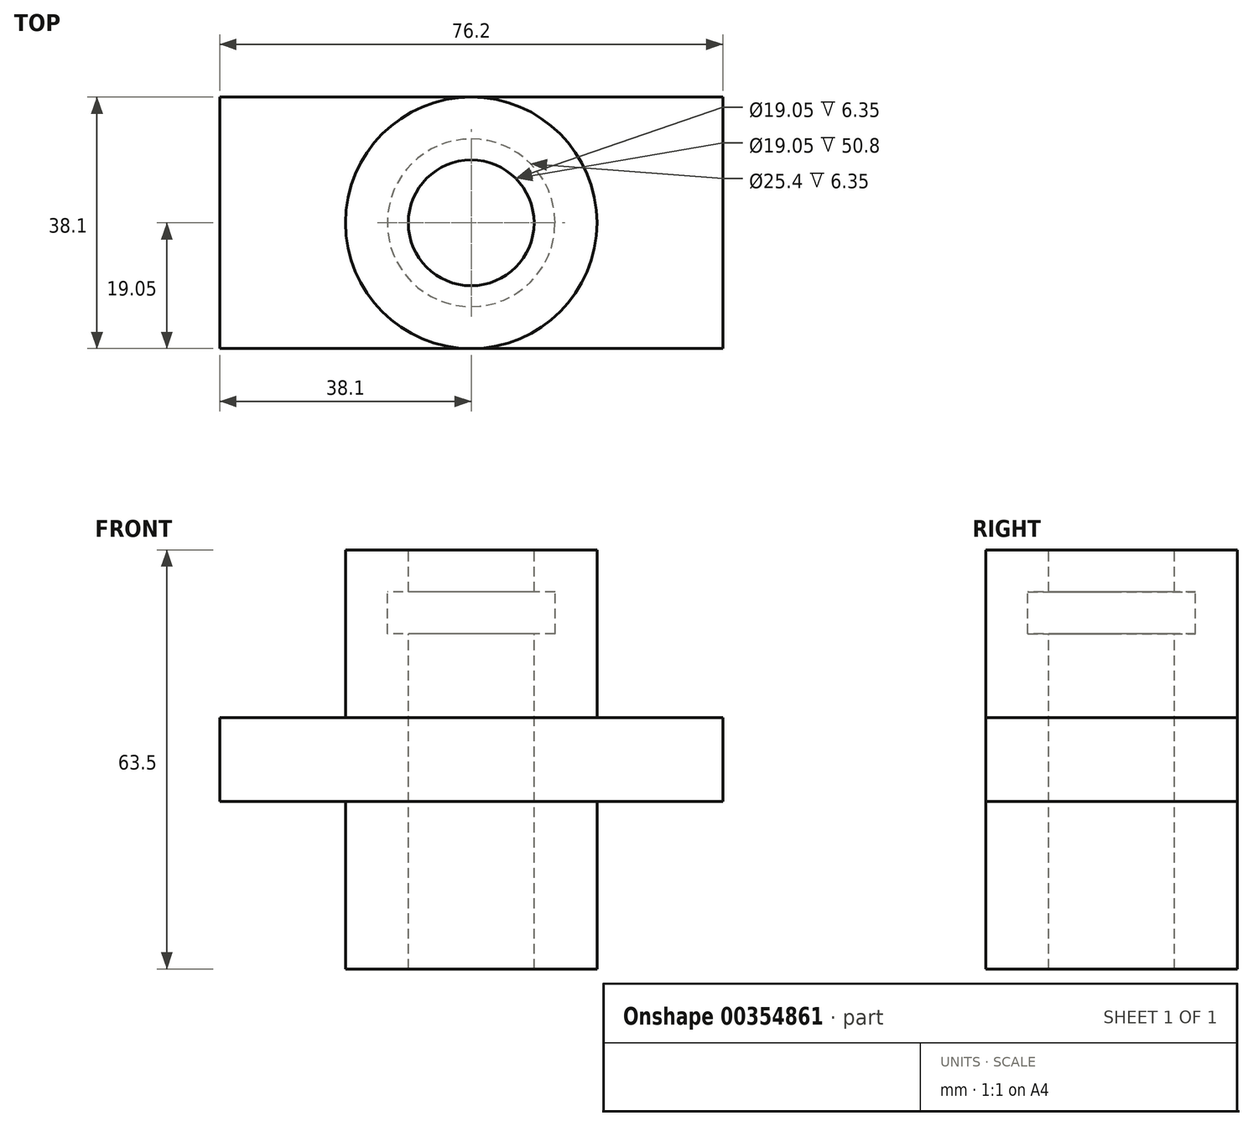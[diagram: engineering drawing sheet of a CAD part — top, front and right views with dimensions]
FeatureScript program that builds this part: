
annotation { "Feature Type Name" : "Feature", "Feature Type Description" : "" }
export const myFeature = defineFeature(function(context is Context, id is Id, definition is map)
    precondition{}
    {
        {
            var Q0;
            Q0=qCreatedBy(makeId("Front.planeOp"),FACE);
            var sketch = newSketch(context, id + "F0", { "sketchPlane" : qUnion([Q0])});
            skLineSegment(sketch, "E0", {"start": v(-9.53, 31.75) * mm, "end": v(-9.52, 25.4) * mm});
            skLineSegment(sketch, "E1", {"start": v(-9.53, 25.4) * mm, "end": v(-12.7, 25.4) * mm});
            skLineSegment(sketch, "E2", {"start": v(-12.7, 25.4) * mm, "end": v(-12.7, 19.05) * mm});
            skLineSegment(sketch, "E3", {"start": v(-12.7, 19.05) * mm, "end": v(-9.53, 19.05) * mm});
            skLineSegment(sketch, "E4", {"start": v(-9.53, 19.05) * mm, "end": v(-9.53, -31.75) * mm});
            skLineSegment(sketch, "E5", {"start": v(-9.53, -31.75) * mm, "end": v(-19.05, -31.75) * mm});
            skLineSegment(sketch, "E6", {"start": v(-19.05, -31.75) * mm, "end": v(-19.05, 31.75) * mm});
            skLineSegment(sketch, "E7", {"start": v(-19.05, 31.75) * mm, "end": v(-9.53, 31.75) * mm});
            skLineSegment(sketch, "E8", {"start": v(0, 58.37) * mm, "end": v(0, -55.1) * mm, "construction": true});
            skSolve(sketch);
        }
        {
            var Q0;
            Q0=makeQuery(id+"F0.imprint","IMPRINT",FACE,{"disambiguationData":[TD([[makeQuery(id+"F0.imprint","IMPRINT",EDGE,{"derivedFrom":sQuery(id+"F0.wireOp",EDGE,"E0")}),-1.0]])]});
            var Q1;
            Q1=sQuery(id+"F0.wireOp",EDGE,"E8");
            revolve(context, id + "F1", {"entities" : qUnion([Q0]), "axis" : qUnion([Q1]), "revolveType" : RevolveType.FULL});
        }
        {
            var Q0;
            Q0=qCreatedBy(makeId("Top.planeOp"),FACE);
            var sketch = newSketch(context, id + "F2", { "sketchPlane" : qUnion([Q0])});
            skLineSegment(sketch, "E9.bottom", {"start": v(-38.1, 19.05) * mm, "end": v(38.1, 19.05) * mm});
            skLineSegment(sketch, "E9.top", {"start": v(-38.1, -19.05) * mm, "end": v(38.1, -19.05) * mm});
            skLineSegment(sketch, "E9.left", {"start": v(-38.1, 19.05) * mm, "end": v(-38.1, -19.05) * mm});
            skLineSegment(sketch, "E9.right", {"start": v(38.1, 19.05) * mm, "end": v(38.1, -19.05) * mm});
            skSolve(sketch);
        }
        {
            var Q0;
            Q0=makeQuery(id+"F2.imprint","IMPRINT",FACE,{"disambiguationData":[TD([[makeQuery(id+"F2.imprint","IMPRINT",EDGE,{"derivedFrom":sQuery(id+"F2.wireOp",EDGE,"E9.bottom")}),-1.0]])]});
            extrude(context, id + "F3", {"entities" : qUnion([Q0]), "operationType" : NewBodyOperationType.ADD, "endBound" : BoundingType.SYMMETRIC, "depth" : 12.7 * mm});
        }
        {
            var Q0;
            Q0=makeQuery(id+"F1.opRevolve","SWEPT_FACE",FACE,{"disambiguationData":[OSD([sQuery(id+"F0.wireOp",EDGE,"E7")])]});
            var sketch = newSketch(context, id + "F4", { "sketchPlane" : qUnion([Q0])});
            skCircle(sketch, "E10", {"center": v(0, 0) * mm, "radius": 9.53 * mm});
            skSolve(sketch);
        }
        {
            var Q0;
            Q0 = qSketchRegion(id + "F4", true);
            extrude(context, id + "F5", {"entities" : qUnion([Q0]), "operationType" : NewBodyOperationType.REMOVE, "endBound" : BoundingType.THROUGH_ALL, "oppositeDirection" : true, "depth" : 25.4 * mm});
        }
    });
